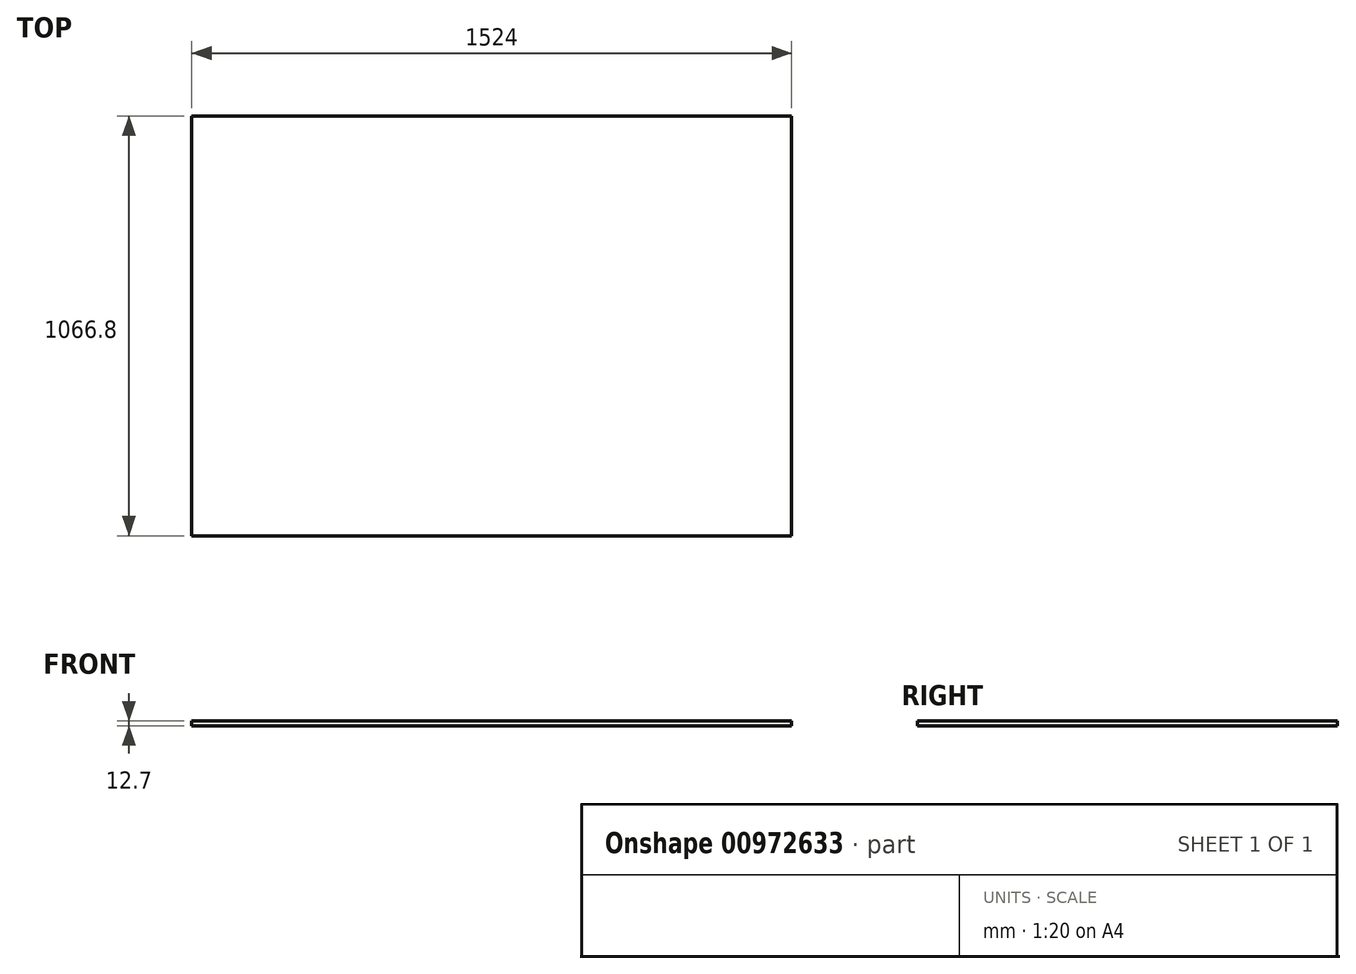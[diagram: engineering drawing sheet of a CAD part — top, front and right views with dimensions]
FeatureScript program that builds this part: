
annotation { "Feature Type Name" : "Feature", "Feature Type Description" : "" }
export const myFeature = defineFeature(function(context is Context, id is Id, definition is map)
    precondition{}
    {
        {
            var Q0;
            Q0=qCreatedBy(makeId("Top.planeOp"),FACE);
            var sketch = newSketch(context, id + "F0", { "sketchPlane" : qUnion([Q0])});
            skLineSegment(sketch, "E0.bottom", {"start": v(-1494.23, 1010.66) * mm, "end": v(29.77, 1010.66) * mm});
            skLineSegment(sketch, "E0.top", {"start": v(-1494.23, -56.14) * mm, "end": v(29.77, -56.14) * mm});
            skLineSegment(sketch, "E0.left", {"start": v(-1494.23, 1010.66) * mm, "end": v(-1494.23, -56.14) * mm});
            skLineSegment(sketch, "E0.right", {"start": v(29.77, 1010.66) * mm, "end": v(29.77, -56.14) * mm});
            skSolve(sketch);
        }
        {
            var Q0;
            Q0=makeQuery(id+"F0.imprint","IMPRINT",FACE,{"disambiguationData":[TD([[makeQuery(id+"F0.imprint","IMPRINT",EDGE,{"derivedFrom":sQuery(id+"F0.wireOp",EDGE,"E0.bottom")}),-1.0]])]});
            extrude(context, id + "F1", {"entities" : qUnion([Q0]), "depth" : 12.7 * mm, "offsetDistance" : 25.4 * mm});
        }
    });
